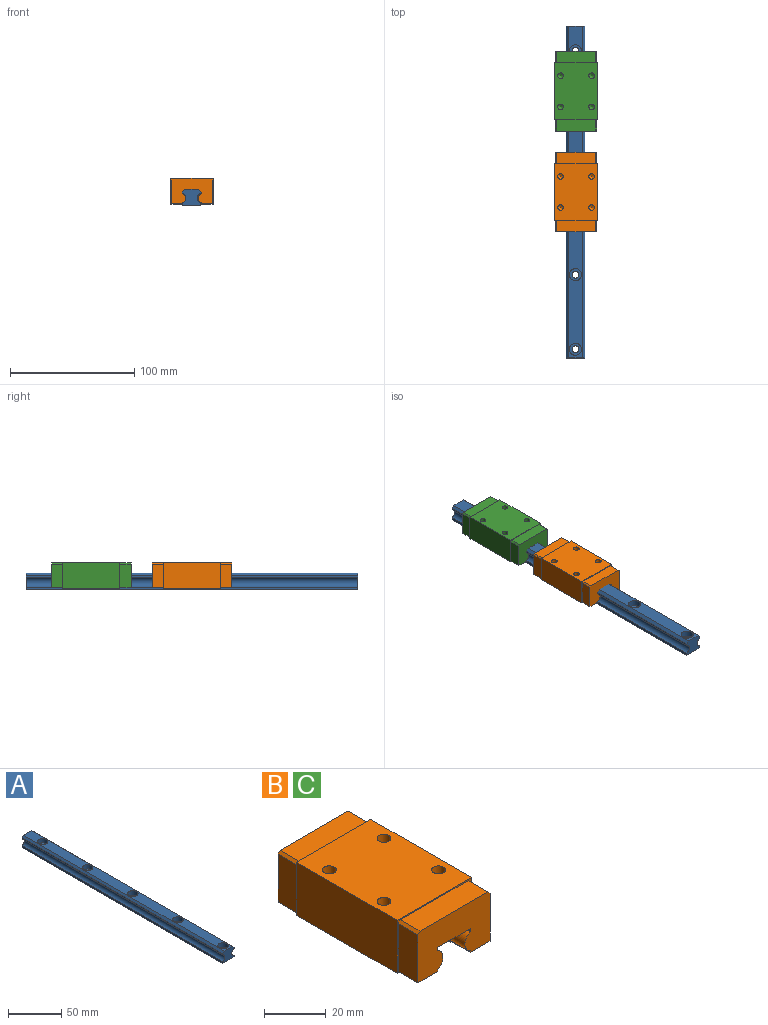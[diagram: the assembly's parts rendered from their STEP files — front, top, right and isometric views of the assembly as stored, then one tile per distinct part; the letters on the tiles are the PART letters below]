
ASSEMBLY  parts=3 mates=4
PART A: 27 faces, bbox 15x267x13.2 mm
  f0: plane 267x15mm, normal (0,0,-1), area 3886.2mm2, adj f5,f6,f10,f11,f14,f17,f20,f23
  f1: plane 267x11mm, normal (0,0,1), area 2563.7mm2, adj f2,f9,f10,f13,f16,f19,f22,f25
  f2: plane 267x2mm, normal (-0.71,0,0.71), area 755.2mm2, adj f1,f3,f10,f26
  f3: plane 267x1.35mm, normal (-1,0,0), area 360.8mm2, adj f2,f4,f10,f26
  f4: cylinder r=4mm len=267mm, axis (0,1,0), area 2765.7mm2, adj f3,f5,f10,f26
  f5: plane 267x2.15mm, normal (-1,0,0), area 574.4mm2, adj f0,f4,f10,f26
  f6: plane 267x2.15mm, normal (1,0,0), area 574.4mm2, adj f0,f7,f10,f26
  f7: cylinder r=4mm len=267mm, axis (0,1,0), area 2765.7mm2, adj f6,f8,f10,f26
  f8: plane 267x1.35mm, normal (1,0,0), area 360.8mm2, adj f7,f9,f10,f26
  f9: plane 267x2mm, normal (0.71,0,0.71), area 755.2mm2, adj f1,f8,f10,f26
  f10: plane 15x13.2mm, normal (0,1,0), area 161mm2, adj f0,f1,f2,f3,f4,f5,f6,f7
  f11: cylinder r=2.75mm len=8.2mm, axis (0,0,1), area 141.7mm2, adj f0,f12
  f12: plane 9.75x9.75mm, normal (0,0,1), area 50.9mm2, adj f11,f13
  f13: cylinder r=4.88mm len=9.75mm, axis (0,0,1), area 153.2mm2, adj f1,f12
  f14: cylinder r=2.75mm len=8.2mm, axis (0,0,1), area 141.7mm2, adj f0,f15
  f15: plane 9.75x9.75mm, normal (0,0,1), area 50.9mm2, adj f14,f16
  f16: cylinder r=4.88mm len=9.75mm, axis (0,0,1), area 153.2mm2, adj f1,f15
  f17: cylinder r=2.75mm len=8.2mm, axis (0,0,1), area 141.7mm2, adj f0,f18
  f18: plane 9.75x9.75mm, normal (0,0,1), area 50.9mm2, adj f17,f19
  f19: cylinder r=4.88mm len=9.75mm, axis (0,0,1), area 153.2mm2, adj f1,f18
  f20: cylinder r=2.75mm len=8.2mm, axis (0,0,1), area 141.7mm2, adj f0,f21
  f21: plane 9.75x9.75mm, normal (0,0,1), area 50.9mm2, adj f20,f22
  f22: cylinder r=4.88mm len=9.75mm, axis (0,0,1), area 153.2mm2, adj f1,f21
  f23: cylinder r=2.75mm len=8.2mm, axis (0,0,1), area 141.7mm2, adj f0,f24
  f24: plane 9.75x9.75mm, normal (0,0,1), area 50.9mm2, adj f23,f25
  f25: cylinder r=4.88mm len=9.75mm, axis (0,0,1), area 153.2mm2, adj f1,f24
  f26: plane 15x13.2mm, normal (0,-1,0), area 161mm2, adj f0,f1,f2,f3,f4,f5,f6,f7
PART B: 38 faces, bbox 34x64x21 mm
  f0: plane 33x20mm, normal (0,1,0), area 543.3mm2, adj f6,f7,f9,f10,f11,f12,f13,f22
  f1: plane 46x9.5mm, normal (0,0,-1), area 437mm2, adj f2,f6,f21,f29
  f2: plane 46x21mm, normal (1,0,0), area 966mm2, adj f1,f3,f21,f29
  f3: plane 46x34mm, normal (0,0,1), area 1500.4mm2, adj f2,f4,f21,f29,f30,f32,f34,f36
  f4: plane 46x21mm, normal (-1,0,0), area 966mm2, adj f3,f5,f21,f29
  f5: plane 46x9.5mm, normal (0,0,-1), area 437mm2, adj f4,f7,f21,f29
  f6: plane 64x1.29mm, normal (-1,0,0), area 73.7mm2, adj f0,f1,f8,f10,f15,f21,f23,f29
  f7: plane 64x1.29mm, normal (1,0,0), area 73.7mm2, adj f0,f5,f8,f11,f14,f21,f22,f29
  f8: plane 33x20mm, normal (0,-1,0), area 543.3mm2, adj f6,f7,f9,f10,f11,f12,f13,f14
  f9: plane 64x1.29mm, normal (-1,0,0), area 82.7mm2, adj f0,f8,f10,f13
  f10: cylinder r=4mm len=64mm, axis (0,1,0), area 607.4mm2, adj f0,f6,f8,f9
  f11: cylinder r=4mm len=64mm, axis (0,1,0), area 607.4mm2, adj f0,f7,f8,f12
  f12: plane 64x1.29mm, normal (1,0,0), area 82.7mm2, adj f0,f8,f11,f13
  f13: plane 64x15mm, normal (0,0,-1), area 960mm2, adj f0,f8,f9,f12
  f14: plane 9x9mm, normal (0,0,-1), area 81mm2, adj f7,f8,f16,f21
  f15: plane 9x9mm, normal (0,0,-1), area 81mm2, adj f6,f8,f20,f21
  f16: plane 19x9mm, normal (-1,0,0), area 171mm2, adj f8,f14,f17,f21
  f17: plane 9x1mm, normal (-0.71,0,0.71), area 12.7mm2, adj f8,f16,f18,f21
  f18: plane 31x9mm, normal (0,0,1), area 279mm2, adj f8,f17,f19,f21
  f19: plane 9x1mm, normal (0.71,0,0.71), area 12.7mm2, adj f8,f18,f20,f21
  f20: plane 19x9mm, normal (1,0,0), area 171mm2, adj f8,f15,f19,f21
  f21: plane 34x21mm, normal (0,-1,0), area 47.5mm2, adj f1,f2,f3,f4,f5,f6,f7,f14
  f22: plane 9x9mm, normal (0,0,-1), area 81mm2, adj f0,f7,f28,f29
  f23: plane 9x9mm, normal (0,0,-1), area 81mm2, adj f0,f6,f24,f29
  f24: plane 19x9mm, normal (1,0,0), area 171mm2, adj f0,f23,f25,f29
  f25: plane 9x1mm, normal (0.71,0,0.71), area 12.7mm2, adj f0,f24,f26,f29
  f26: plane 31x9mm, normal (0,0,1), area 279mm2, adj f0,f25,f27,f29
  f27: plane 9x1mm, normal (-0.71,0,0.71), area 12.7mm2, adj f0,f26,f28,f29
  f28: plane 19x9mm, normal (-1,0,0), area 171mm2, adj f0,f22,f27,f29
  f29: plane 34x21mm, normal (0,1,0), area 47.5mm2, adj f1,f2,f3,f4,f5,f6,f7,f22
  f30: cylinder r=2.25mm len=10.4mm, axis (0,0,1), area 147mm2, adj f3,f31
  f31: cone r=0mm half-angle=59deg, axis (0,0,1), area 18.6mm2, adj f30
  f32: cylinder r=2.25mm len=10.4mm, axis (0,0,1), area 147mm2, adj f3,f33
  f33: cone r=0mm half-angle=59deg, axis (0,0,1), area 18.6mm2, adj f32
  f34: cylinder r=2.25mm len=10.4mm, axis (0,0,1), area 147mm2, adj f3,f35
  f35: cone r=0mm half-angle=59deg, axis (0,0,1), area 18.6mm2, adj f34
  f36: cylinder r=2.25mm len=10.4mm, axis (0,0,1), area 147mm2, adj f3,f37
  f37: cone r=0mm half-angle=59deg, axis (0,0,1), area 18.6mm2, adj f36
PART C: same geometry as B
PLACE A at identity fixed
PLACE B t=(0.41,-133.5,1)mm
PLACE C rot(axis=(0,-1,0),0deg) t=(0.41,-52.5,1)mm
MATE cylindrical A.f4 <-> B.f11  axis (0,1,0) through (-8.59,-133.5,6)mm
MATE cylindrical C.f11 <-> A.f4  axis (0,1,0) through (-8.59,-84.5,6)mm
MATE parallel B.f13 <-> A.f1  axis (0,0,-1) through (0.41,-165.5,11)mm
MATE parallel A.f14 <-> C.f13  axis (0,0,1) through (0,-80,13.2)mm
